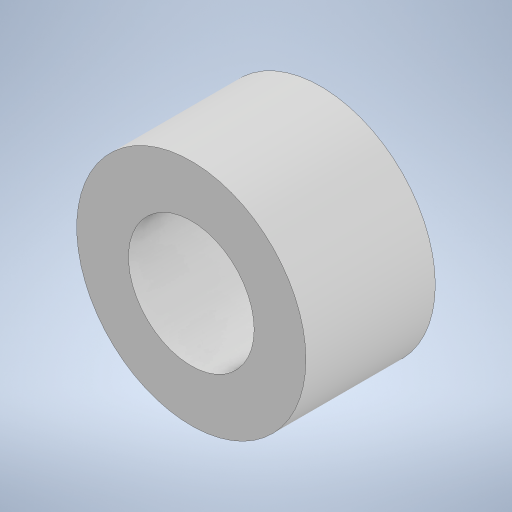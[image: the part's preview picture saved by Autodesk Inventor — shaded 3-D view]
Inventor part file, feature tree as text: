
AUTODESK INVENTOR PART (.ipt)
format: ipt  version: 2024 (Build 280153000, 153)  size: 208,896 bytes
history: native  units: in
note: dims shown in document units (in); Inventor stores cm internally (conversion verified against a paired STEP export)
features: extrude x1, sketch x1
ambient origin geometry x8: Origin, YZ Plane, XZ Plane, XY Plane, X Axis, Y Axis, Z Axis, Center Point
bodies: Solid1 (feature_tree)
feature tree (2):
  extrude  "Extrusion1"  Depth=0.175in
  sketch  "Sketch1"  dims[d0=0.17in d1=0.07in d2=0.175in d3=0.0in]
